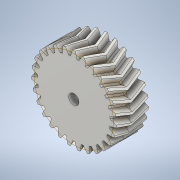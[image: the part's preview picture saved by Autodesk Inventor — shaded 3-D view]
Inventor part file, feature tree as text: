
AUTODESK INVENTOR PART (.ipt)
format: ipt  version: 2020 (Build 240168000, 168)  size: 742,400 bytes
history: native  units: mm (DEFAULTED — no unit token found)
features: other x4, extrude x3, plane x3, sketch x3, mirror x1
ambient origin geometry x8: Origin, YZ Plane, XZ Plane, XY Plane, X Axis, Y Axis, Z Axis, Center Point
bodies: Solid1 (feature_tree)
feature tree (14):
  extrude  "Extrusion1"  Depth=5.0mm TaperAngle=0.0deg
  plane  "Work Plane2"
  plane  "Work Plane8"
  plane  "Work Plane9"
  other  "Spur Gear"
  mirror  "Mirror1"
  extrude  "Extrusion2"  Depth=10.0mm TaperAngle=0.0deg
  sketch  "Sketch1"  dims[d0=26.262248mm d1=5.0mm d2=0.0mm]
  sketch  "Sketch2"  dims[d3=24.545455mm d4=10.0mm d5=0.0mm]
  other  "Srf1"
  other  "Srf2"
  sketch  "Sketch3"  dims[d16=25.0mm d17=0.0mm d34=1.163553mm d39=0.0mm d41=0.0mm d43=25.0mm d46=25.0mm d47=0.0mm d48=0.0mm d49=3.2mm d50=10.0mm d51=0.0mm]
  other  "Pitch Diameter"
  extrude  "ExtrusionSrf2"  Depth=10.0mm TaperAngle=0.0deg
